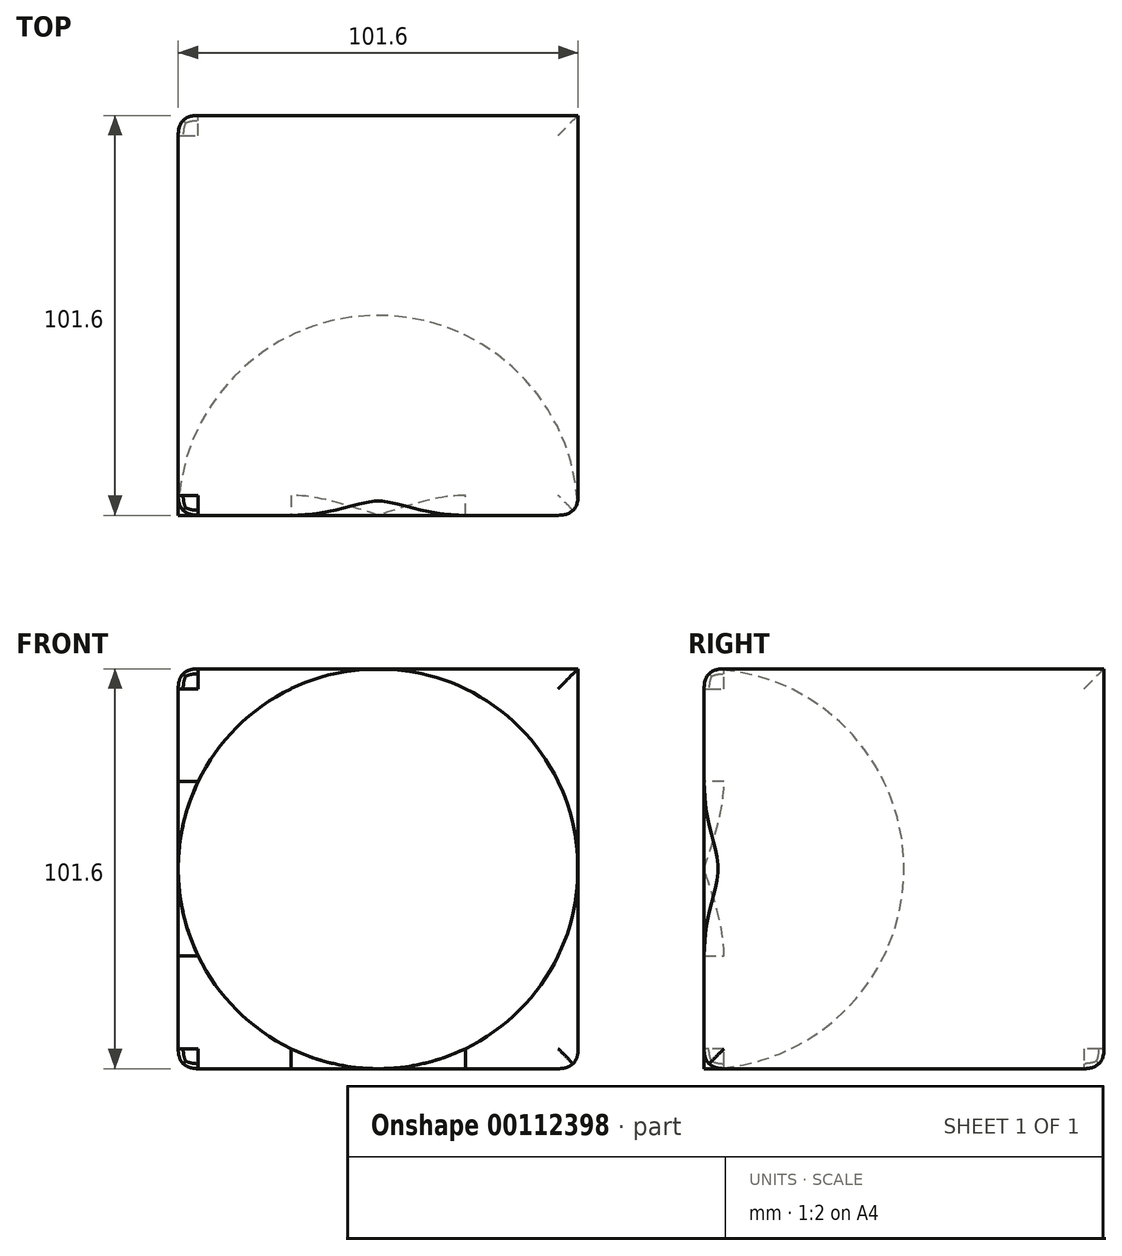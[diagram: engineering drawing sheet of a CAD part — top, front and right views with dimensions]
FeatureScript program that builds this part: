
annotation { "Feature Type Name" : "Feature", "Feature Type Description" : "" }
export const myFeature = defineFeature(function(context is Context, id is Id, definition is map)
    precondition{}
    {
        {
            var Q0;
            Q0=qCreatedBy(makeId("Front.planeOp"),FACE);
            var sketch = newSketch(context, id + "F0", { "sketchPlane" : qUnion([Q0])});
            skLineSegment(sketch, "E0.bottom", {"start": v(-101.6, 0) * mm, "end": v(0, 0) * mm});
            skLineSegment(sketch, "E0.top", {"start": v(-101.6, 101.6) * mm, "end": v(0, 101.6) * mm});
            skLineSegment(sketch, "E0.left", {"start": v(-101.6, 0) * mm, "end": v(-101.6, 101.6) * mm});
            skLineSegment(sketch, "E0.right", {"start": v(0, 0) * mm, "end": v(0, 101.6) * mm});
            skSolve(sketch);
        }
        {
            var Q0;
            Q0=makeQuery(id+"F0.imprint","IMPRINT",FACE,{"disambiguationData":[TD([[makeQuery(id+"F0.imprint","IMPRINT",EDGE,{"derivedFrom":sQuery(id+"F0.wireOp",EDGE,"E0.bottom")}),1.0]])]});
            extrude(context, id + "F1", {"entities" : qUnion([Q0]), "depth" : 101.6 * mm});
        }
        {
            var Q0;
            Q0=makeQuery(id+"F1.opExtrude","CAP_FACE",FACE,{"disambiguationData":[OSD([sQuery(id+"F0.wireOp",EDGE,"E0.bottom"),sQuery(id+"F0.wireOp",EDGE,"E0.top"),sQuery(id+"F0.wireOp",EDGE,"E0.left"),sQuery(id+"F0.wireOp",EDGE,"E0.right")])],"isStart":false});
            cPlane(context, id + "F2", {"entities" : qUnion([Q0]), "cplaneType" : CPlaneType.OFFSET, "offset" : 0 * mm, "width" : 152.4 * mm, "height" : 152.4 * mm});
        }
        {
            var Q0;
            Q0=qCreatedBy(id+"F2.planeOp",FACE);
            var sketch = newSketch(context, id + "F3", { "sketchPlane" : qUnion([Q0])});
            skCircle(sketch, "E1", {"center": v(-50.8, 50.8) * mm, "radius": 50.8 * mm});
            skPoint(sketch, "E1.centerSnap0", {"position": v(-101.6, 50.8) * mm});
            skPoint(sketch, "E1.centerSnap1", {"position": v(-50.8, 0) * mm});
            skLineSegment(sketch, "E2", {"start": v(-101.6, 50.8) * mm, "end": v(0, 50.8) * mm});
            skSolve(sketch);
        }
        {
            var Q0;
            {var subQ0=sQuery(id+"F3.wireOp",EDGE,"E2");Q0=makeQuery(id+"F3.imprint","IMPRINT",FACE,{"disambiguationData":[TD([[makeQuery(id+"F3.imprint","IMPRINT",EDGE,{"derivedFrom":subQ0}),1.0]])]});}
            var Q1;
            Q1=sQuery(id+"F3.wireOp",EDGE,"E2");
            revolve(context, id + "F4", {"entities" : qUnion([Q0]), "axis" : qUnion([Q1]), "revolveType" : RevolveType.FULL});
        }
        {
            var Q0;
            Q0=makeQuery(id+"F4.opRevolve","SWEPT_BODY",BODY,{"disambiguationData":[OSD([sQuery(id+"F3.wireOp",EDGE,"E1"),sQuery(id+"F3.wireOp",EDGE,"E2")])]});
            var Q1;
            Q1=makeQuery(id+"F1.opExtrude","SWEPT_BODY",BODY,{"disambiguationData":[OSD([sQuery(id+"F0.wireOp",EDGE,"E0.bottom"),sQuery(id+"F0.wireOp",EDGE,"E0.top"),sQuery(id+"F0.wireOp",EDGE,"E0.left"),sQuery(id+"F0.wireOp",EDGE,"E0.right")])]});
            booleanBodies(context, id + "F5", {"operationType" : BooleanOperationType.SUBTRACTION, "tools" : qUnion([Q0]), "targets" : qUnion([Q1]), "offsetAll" : true});
        }
        {
            var Q0;
            {var subQ0=sQuery(id+"F0.wireOp",EDGE,"E0.left");var subQ1=sQuery(id+"F0.wireOp",EDGE,"E0.top");Q0=makeQuery(id+"F5.opBoolean","SPLIT",EDGE,{"disambiguationData":[TD([makeQuery(id+"F1.opExtrude","SWEPT_FACE",FACE,{"disambiguationData":[OSD([subQ0])]})])],"derivedFrom":makeQuery(id+"F1.opExtrude","CAP_EDGE",EDGE,{"disambiguationData":[OSD([subQ1])],"isStart":false})});}
            var Q1;
            {var subQ0=sQuery(id+"F0.wireOp",EDGE,"E0.right");var subQ1=sQuery(id+"F0.wireOp",EDGE,"E0.top");Q1=makeQuery(id+"F5.opBoolean","SPLIT",EDGE,{"disambiguationData":[TD([makeQuery(id+"F1.opExtrude","SWEPT_FACE",FACE,{"disambiguationData":[OSD([subQ1])]})])],"derivedFrom":makeQuery(id+"F1.opExtrude","CAP_EDGE",EDGE,{"disambiguationData":[OSD([subQ0])],"isStart":false})});}
            var Q2;
            Q2=makeQuery(id+"F1.opExtrude","SWEPT_FACE",FACE,{"disambiguationData":[OSD([sQuery(id+"F0.wireOp",EDGE,"E0.bottom")])]});
            var Q3;
            Q3=makeQuery(id+"F1.opExtrude","SWEPT_FACE",FACE,{"disambiguationData":[OSD([sQuery(id+"F0.wireOp",EDGE,"E0.left")])]});
            fillet(context, id + "F6", {"entities" : qUnion([Q0, Q1, Q2, Q3]), "radius" : 5.08 * mm, "tangentPropagation" : true, "rho" : 0.5, "crossSection" : FilletCrossSection.CONIC, "allowEdgeOverflow" : false});
        }
    });
